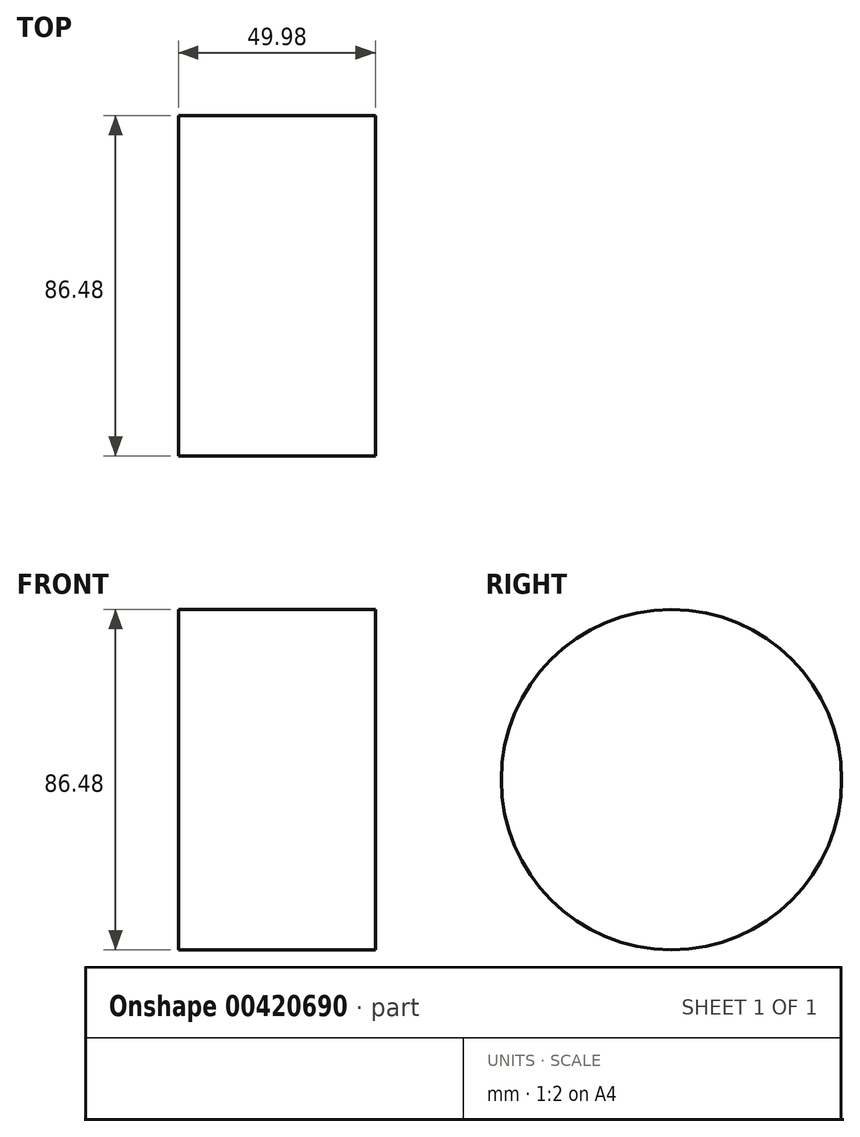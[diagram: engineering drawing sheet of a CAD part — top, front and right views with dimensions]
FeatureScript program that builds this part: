
annotation { "Feature Type Name" : "Feature", "Feature Type Description" : "" }
export const myFeature = defineFeature(function(context is Context, id is Id, definition is map)
    precondition{}
    {
        {
            var Q0;
            Q0=qCreatedBy(makeId("Front.planeOp"),FACE);
            var sketch = newSketch(context, id + "F0", { "sketchPlane" : qUnion([Q0])});
            skLineSegment(sketch, "E0", {"start": v(-489.5, 0) * mm, "end": v(382.18, 0) * mm, "construction": true});
            skLineSegment(sketch, "E1", {"start": v(0, 0) * mm, "end": v(0, 43.24) * mm});
            skLineSegment(sketch, "E2", {"start": v(0, 43.24) * mm, "end": v(49.98, 43.24) * mm});
            skLineSegment(sketch, "E3", {"start": v(49.98, 39.12) * mm, "end": v(49.98, 0) * mm});
            skLineSegment(sketch, "E4", {"start": v(49.98, 0) * mm, "end": v(0, 0) * mm});
            skLineSegment(sketch, "E5", {"start": v(49.98, 39.12) * mm, "end": v(49.98, 43.24) * mm});
            skSolve(sketch);
        }
        {
            var Q0;
            Q0=makeQuery(id+"F0.imprint","IMPRINT",FACE,{"disambiguationData":[TD([[makeQuery(id+"F0.imprint","IMPRINT",EDGE,{"derivedFrom":sQuery(id+"F0.wireOp",EDGE,"E1")}),-1.0]])]});
            var Q1;
            Q1=sQuery(id+"F0.wireOp",EDGE,"E0");
            revolve(context, id + "F1", {"entities" : qUnion([Q0]), "axis" : qUnion([Q1]), "revolveType" : RevolveType.FULL});
        }
    });
